# Revit family: Faucet-Lavatory-KOHLER-Artifacts-K-72763_1
name_source: partatom
category: Plumbing Fixtures
revit_build: Autodesk Revit 2015 (Build: 20140606_1530(x64)
units: mm (PartAtom-declared; Revit-internal decimal feet)

## types (5) — shared parameters
ADA Compliant = No
Assembly Code = D2010
CW Connection = Yes
Cold Water Inlet = Cold Water Inlet
Date Modified = 10/19/2018
Default Elevation = 36"
Description = Gentleman's single-handle bathroom sink faucet
Drain Included = Yes
Faucet Hole Spacing = 0"
Flow Rate = 1 GPM
HW Connection = Yes
Handle Clearance = 3 7/16"
Height = 13 1/16"
Hot Water Inlet = Hot Water Inlet
Length = 9 1/4"
Manufacturer = KOHLER Co.
MasterFormat 1995 = 15410
MasterFormat 2004 = 22.41.39
Material = Premium Metal Construction
Pressure = 60.00 psi
Product Documentation Link = http://www.us.kohler.com
Product Name = Artifacts
Product Page URL = http://www.us.kohler.com
Spout Reach = 7 5/16"
URL = https://www.us.kohler.com
Vent Connection = No
Waste Connection = No
Waste Water Outlet = Waste Water Outlet
Width = 2 5/8"

## per-type parameters (varying)
| type | Finish | Model | Type |
| CP - Polished Chrome | Kohler-Metal-CP-Polished_Chrome | K-72763-9M-CP | 1 |
| SN - Vibrant Polished Nickel | Kohler-Metal-SN-Vibrant_Polished_Nickel | K-72763-9M-SN | 2 |
| VS - Vibrant Stainless | Kohler-Metal-VS-Vibrant_Stainless | K-72763-9M-VS | 3 |
| 2BZ - Oil-Rubbed Bronze | Kohler-Metal-2BZ-Oil_Rubbed_Bronze | K-72763-9M-2BZ | 4 |
| VNT - Vintage Nickel | Kohler-Metal-VNT-Vintage_Nickel | K-72763-9M-VNT | 5 |

## geometry (parser evidence)
native form markers: Sweep x4
no freeform markers — native parametric forms only
